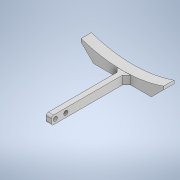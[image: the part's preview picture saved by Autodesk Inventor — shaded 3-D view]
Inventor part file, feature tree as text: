
AUTODESK INVENTOR PART (.ipt)
format: ipt  version: 2020 (Build 240168000, 168)  size: 177,664 bytes
history: native  units: mm
features: extrude x3, sketch x3, chamfer x2, fillet x1
ambient origin geometry x8: Origin, YZ Plane, XZ Plane, XY Plane, X Axis, Y Axis, Z Axis, Center Point
bodies: Solide1 (feature_tree)
feature tree (9):
  extrude  "Extrusion1"  Depth=15.0mm
  extrude  "Extrusion2"  Depth=80.0mm
  extrude  "Extrusion8"  Depth=10.0mm TaperAngle=0.0deg
  chamfer  "Chanfrein1"  Distance=5.0mm
  chamfer  "Chanfrein2"  Distance=80.0mm
  fillet  "Congé1"  Radius=72.9mm
  sketch  "Esquisse1"
  sketch  "Esquisse2"
  sketch  "Esquisse8"
